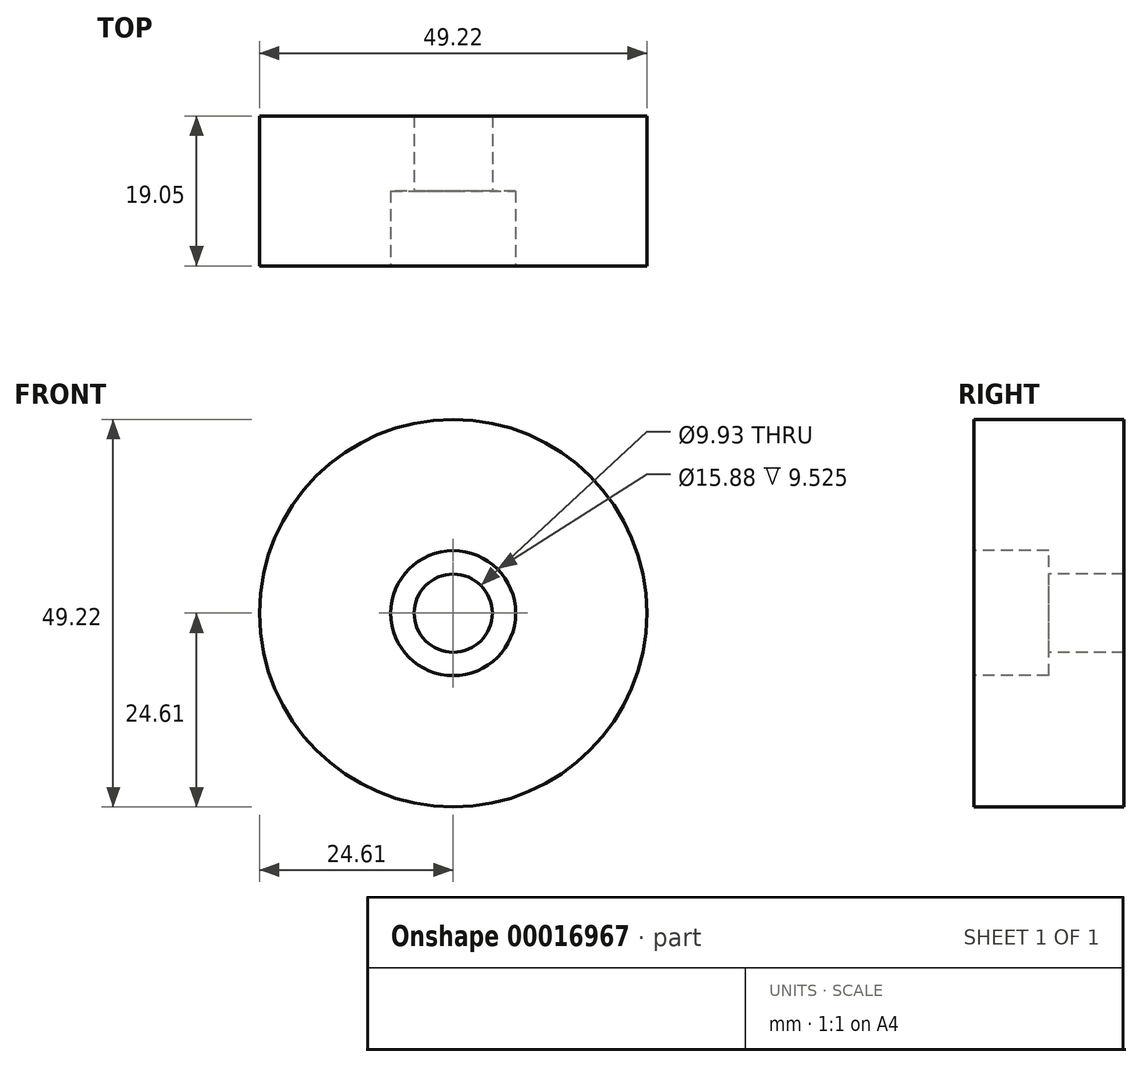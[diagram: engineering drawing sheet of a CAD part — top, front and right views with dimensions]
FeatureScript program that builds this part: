
annotation { "Feature Type Name" : "Feature", "Feature Type Description" : "" }
export const myFeature = defineFeature(function(context is Context, id is Id, definition is map)
    precondition{}
    {
        {
            var Q0;
            Q0=qCreatedBy(makeId("Front.planeOp"),FACE);
            var sketch = newSketch(context, id + "F0", { "sketchPlane" : qUnion([Q0])});
            skCircle(sketch, "E0", {"center": v(0, 0) * mm, "radius": 24.6 * mm});
            skSolve(sketch);
        }
        {
            var Q0;
            Q0=makeQuery(id+"F0.imprint","IMPRINT",FACE,{"disambiguationData":[TD([[makeQuery(id+"F0.imprint","IMPRINT",EDGE,{"derivedFrom":sQuery(id+"F0.wireOp",EDGE,"E0")}),1.0]])]});
            extrude(context, id + "F1", {"entities" : qUnion([Q0]), "depth" : 19.05 * mm});
        }
        {
            var Q0;
            Q0=makeQuery(id+"F1.opExtrude","CAP_FACE",FACE,{"disambiguationData":[OSD([sQuery(id+"F0.wireOp",EDGE,"E0")])],"isStart":false});
            var sketch = newSketch(context, id + "F2", { "sketchPlane" : qUnion([Q0])});
            skPoint(sketch, "E1", {"position": v(0, 0) * mm});
            skSolve(sketch);
        }
        {
            var Q0;
            Q0=sQuery(id+"F2.wireOp",VERTEX,"E1");
            var Q1;
            Q1=makeQuery(id+"F1.opExtrude","SWEPT_BODY",BODY,{"disambiguationData":[OSD([sQuery(id+"F0.wireOp",EDGE,"E0")])]});
            hole(context, id + "F3", {"style" : HoleStyle.C_BORE, "holeDiameter" : 9.93 * mm, "cBoreDiameter" : 15.88 * mm, "cBoreDepth" : 9.52 * mm, "endStyle" : HoleEndStyle.THROUGH, "locations" : qUnion([Q0]), "scope" : qUnion([Q1])});
        }
    });
